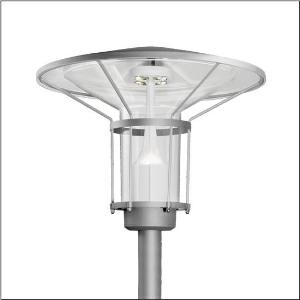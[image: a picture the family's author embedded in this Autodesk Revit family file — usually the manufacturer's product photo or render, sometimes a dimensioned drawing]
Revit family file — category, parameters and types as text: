
# Revit family: laterne_classic_iq___st1_2a_5xa5245mf14h_178e
name_source: partatom
category: Lighting Fixtures
units: mm (PartAtom-declared; Revit-internal decimal feet)

## family parameters
Cut with Voids When Loaded = No
Host = Face
Light Source = No
Part Type = Normal
Room Calculation Point = No
Round Connector Dimension = Use Diameter
Shared = No

## types (1)
- --- (1 x LED, 1380 lm, 11.8 W, 2700K)
    Apparent Load = 12 VA
    CIE Flux Codes = 21 60 93 97 100
    Color Rendering = 70
    Color Temperature = 2700K
    Default Elevation = 1800 mm
    Description = Lantern Classic iQ, mast luminaire, Module 540 iQ-SR, primary light control with 3 zone facetted reflector, of plastic, silver coated, highly specular, structured, primary optical cover: cover, of PMMA, transparent, light distribution: ST1.2a, light emission: direct distribution, primary light characteristic: asymmetric, installation type: post-top, LED, High Power LED, rated luminous flux: 1.380lm, luminous efficacy: 117lm/W, light colour: 727, colour temperature: 2700K, control gear: ECG iQ, control: presetting dimming logarithmic, Street-Remote, Auto-Match, Temp-Guard, Lumen-Switch, Night-Set, Smart-Wire, Light-Fading, Desk-Remote (wireless, voltage-free reading and setting of iQ features in the workshop via application-optimized NFC function/RFID function), optimised constant luminous flux control (CLO 2.0), with terminal, 6-pole, max. 2.5mm², mains connection: 230..240V, AC, 50/60Hz, start of lifetime: 12W, end of service life: 12W, reduction: 6W, luminaire housing, upper part, of glass-fibre reinforced polyester, coated, Siteco® metallic grey (DB 702S), diameter: 750mm, height: 596mm, spigot size: d x l = 76 x 70mm (post-top) | with reducer (optional accessory) 60 x 70mm, post-top mast mounting element, of diecast aluminium, coated, Siteco® metallic grey (DB 702S), Module 540 iQ-SR, traffic white (RAL 9016), equipment: standard, protection rating (complete): IP65, insulation class (complete): insulation class II (safety insulation), certification: CE, ENEC, VDE, packaging unit: 1 piece

Light Distribution: ST1.2a
    Height = 596 mm
    Lamp = 1 x LED
    Lamp Light Flux = 1380 lm
    Lamp Power = 11.8 W
    Lamp count = 1
    Length = 750 mm
    Luminous efficacy = 117 lm/W
    Manufacturer = Siteco
    ModVariant = No
    Model = 5XA5245MF14H
    Number of Poles = 1
    OnlyDefault = Yes
    Power Factor = 1
    Product Name = Laterne Classic iQ | ST1.2a
    Product group = mast luminaire | pylon top
    ProductGroupID = 6100
    Protection Class = Protection class II
    Protection Degree = IP 65
    RLX_Detail_Level = 1
    RLX_Emergency_Light_Flux = 0 lm
    RLX_Emergency_Type = 0
    RLX_Emergency_Type_DB = No
    RlxData = <blob elided: 91569 chars, md5=40393017>
    Socket = socket
    Standby Power = 0 W
    System Light Flux = 1380 lm
    System Power = 12 W
    Type Comments = factory setting: luminous flux: 100 % | dim-lin: 254 | 472 mA
    Type Image = l_1006052.jpg
    URL = http://relux.com
    VarID = @adj_103499
    Voltage = 0 V
    Weight = 0.00 kg
    Width = 0 mm  [stored 0 ft]

note: [stored X ft] marks values corroborated as IEEE doubles in the binary element streams (Revit-internal decimal feet)

## geometry (parser evidence)
native form markers: Blend x4, Sweep x10
no freeform markers — native parametric forms only
